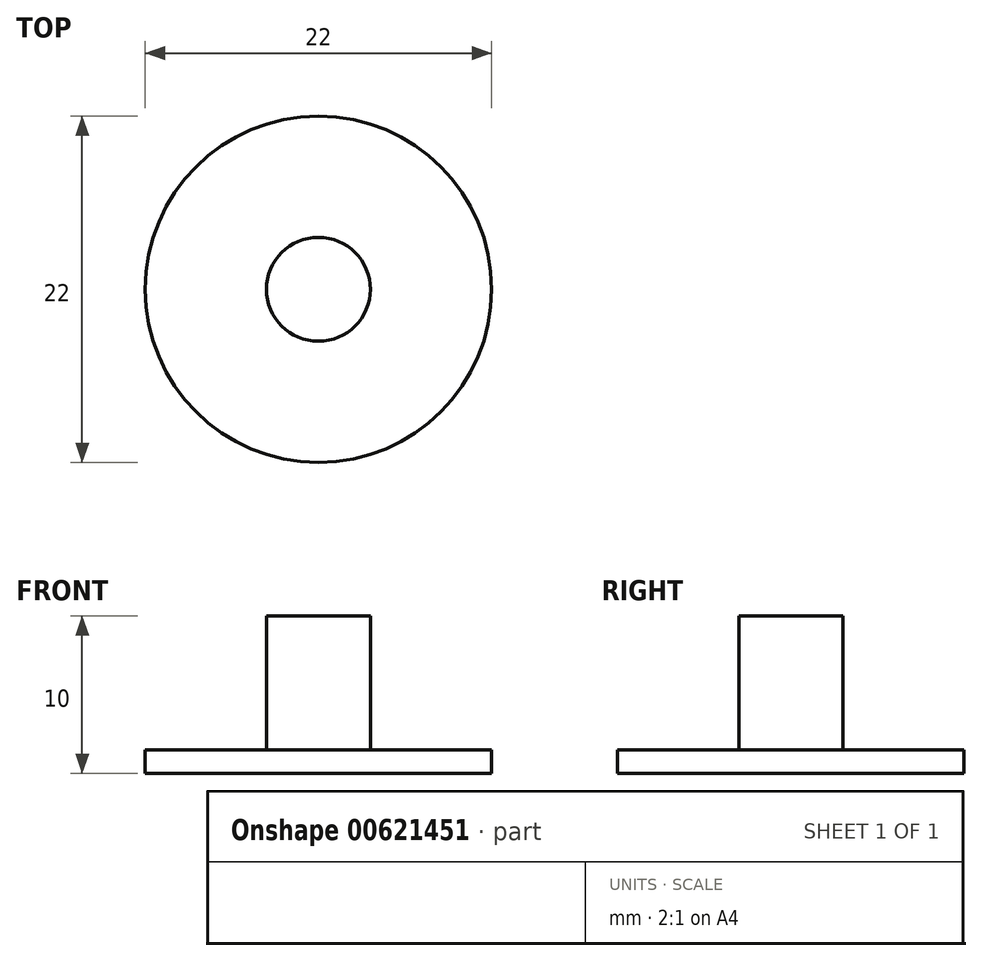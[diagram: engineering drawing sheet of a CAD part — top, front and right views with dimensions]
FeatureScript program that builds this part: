
annotation { "Feature Type Name" : "Feature", "Feature Type Description" : "" }
export const myFeature = defineFeature(function(context is Context, id is Id, definition is map)
    precondition{}
    {
        {
            var Q0;
            Q0=qCreatedBy(makeId("Top.planeOp"),FACE);
            var sketch = newSketch(context, id + "F0", { "sketchPlane" : qUnion([Q0])});
            skCircle(sketch, "E0", {"center": v(0, 0) * mm, "radius": 11 * mm});
            skSolve(sketch);
        }
        {
            var Q0;
            Q0=makeQuery(id+"F0.imprint","IMPRINT",FACE,{"disambiguationData":[TD([[makeQuery(id+"F0.imprint","IMPRINT",EDGE,{"derivedFrom":sQuery(id+"F0.wireOp",EDGE,"E0")}),1.0]])]});
            extrude(context, id + "F1", {"entities" : qUnion([Q0]), "depth" : 1.5 * mm, "offsetDistance" : 25 * mm});
        }
        {
            var Q0;
            Q0=qCreatedBy(makeId("Top.planeOp"),FACE);
            var sketch = newSketch(context, id + "F2", { "sketchPlane" : qUnion([Q0])});
            skCircle(sketch, "E1", {"center": v(0, 0) * mm, "radius": 3.3 * mm});
            skSolve(sketch);
        }
        {
            var Q0;
            Q0=makeQuery(id+"F2.imprint","IMPRINT",FACE,{"disambiguationData":[TD([[makeQuery(id+"F2.imprint","IMPRINT",EDGE,{"derivedFrom":sQuery(id+"F2.wireOp",EDGE,"E1")}),1.0]])]});
            extrude(context, id + "F3", {"entities" : qUnion([Q0]), "operationType" : NewBodyOperationType.ADD, "depth" : 10 * mm, "offsetDistance" : 25 * mm});
        }
    });
